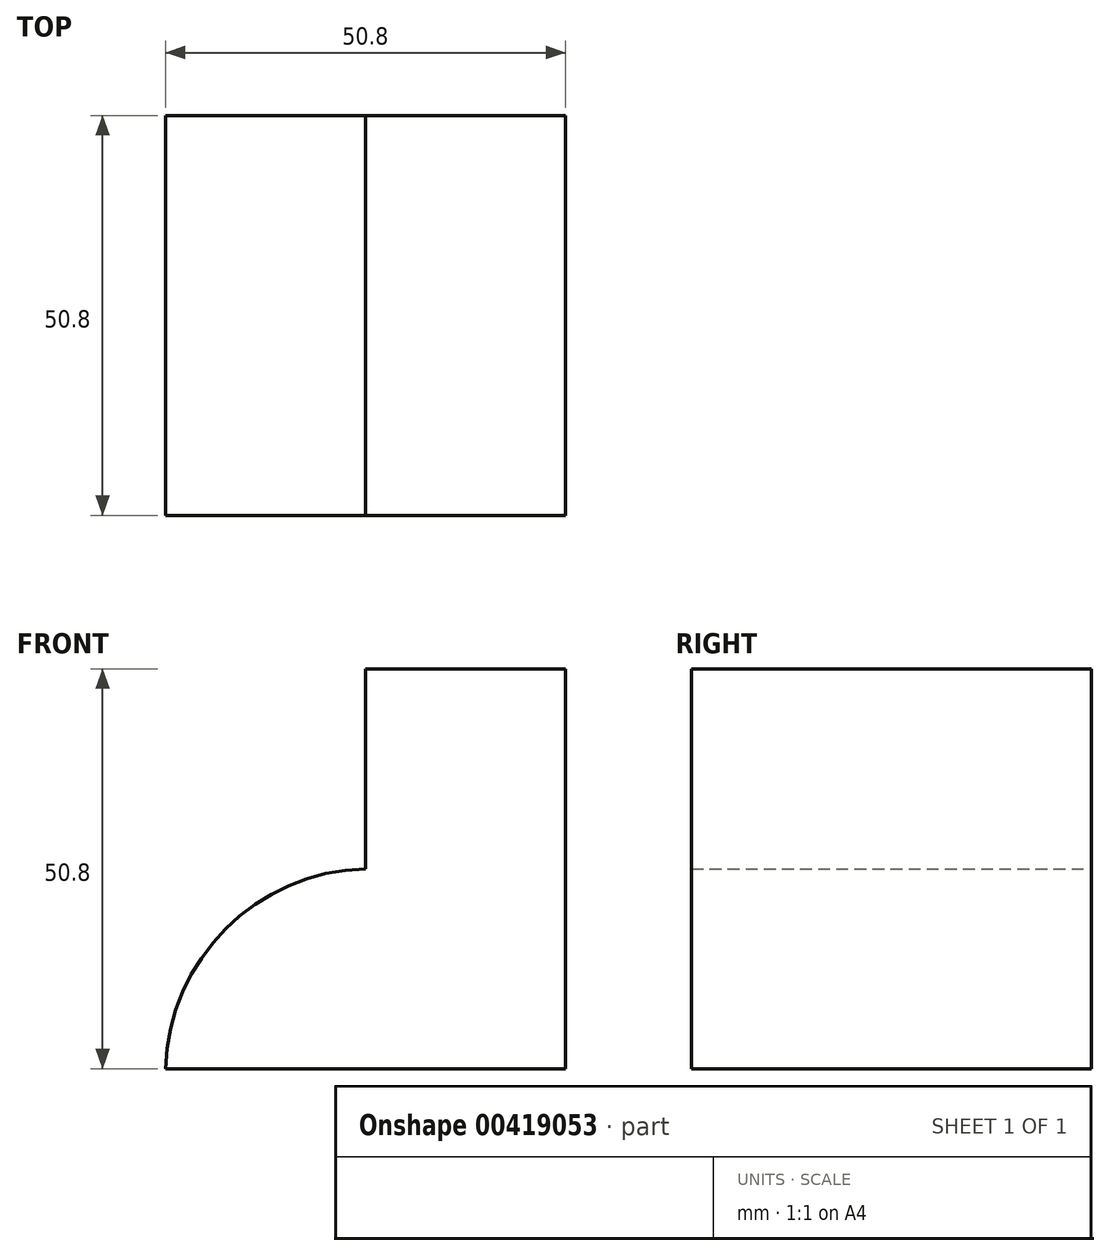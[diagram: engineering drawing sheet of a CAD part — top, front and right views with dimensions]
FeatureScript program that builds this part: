
annotation { "Feature Type Name" : "Feature", "Feature Type Description" : "" }
export const myFeature = defineFeature(function(context is Context, id is Id, definition is map)
    precondition{}
    {
        {
            var Q0;
            Q0=qCreatedBy(makeId("Front.planeOp"),FACE);
            var sketch = newSketch(context, id + "F0", { "sketchPlane" : qUnion([Q0])});
            skLineSegment(sketch, "E0", {"start": v(0, 0) * mm, "end": v(-50.8, 0) * mm});
            skLineSegment(sketch, "E1", {"start": v(0, 0) * mm, "end": v(0, 50.8) * mm});
            skLineSegment(sketch, "E2", {"start": v(0, 50.8) * mm, "end": v(-25.4, 50.8) * mm});
            skLineSegment(sketch, "E3", {"start": v(-25.4, 50.8) * mm, "end": v(-25.4, 25.4) * mm});
            skArc(sketch, "E4", {"start": v(-24.01, 25.4) * mm, "mid": v(-42.67, 18.25) * mm, "end": v(-50.8, 0) * mm});
            skSolve(sketch);
        }
        {
            var Q0;
            Q0 = qSketchRegion(id + "F0", true);
            extrude(context, id + "F1", {"entities" : qUnion([Q0]), "depth" : 50.8 * mm});
        }
    });
